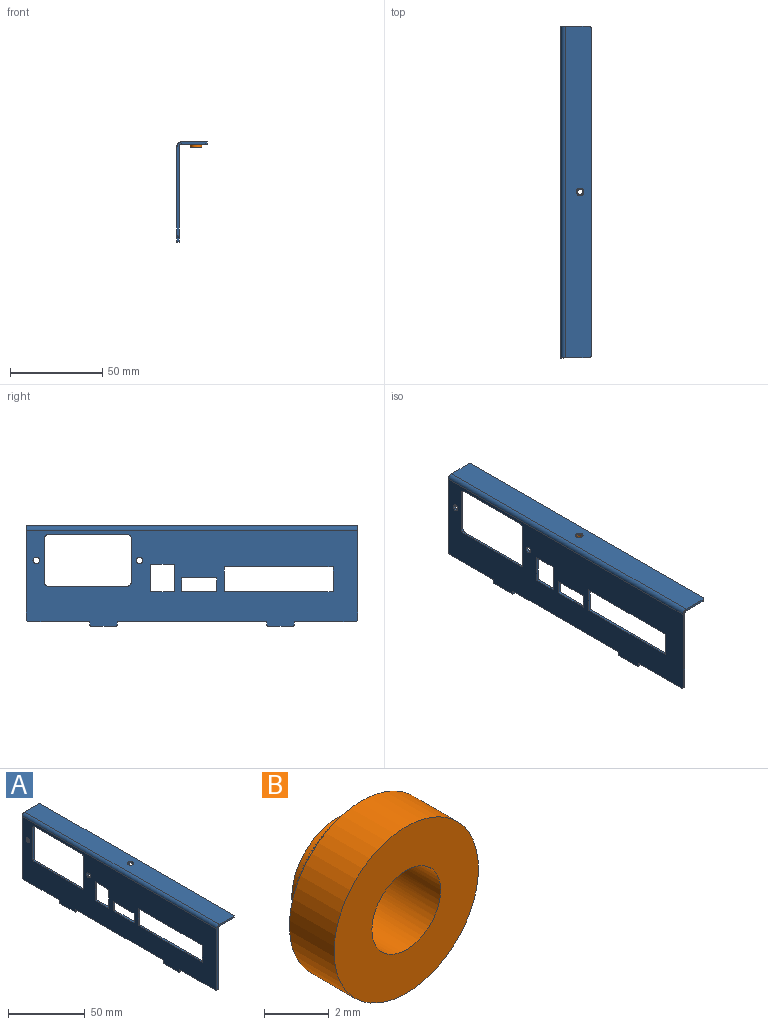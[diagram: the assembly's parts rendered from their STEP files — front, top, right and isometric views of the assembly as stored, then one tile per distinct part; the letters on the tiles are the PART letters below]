
ASSEMBLY  parts=2 mates=1
PART A: 53 faces, bbox 16.4x180x54.3 mm
  f0: plane 15x1.2mm, normal (0,1,0), area 18mm2, adj f1,f32,f33,f34
  f1: plane 12.7x1.2mm, normal (0,0,1), area 15.2mm2, adj f0,f2,f33,f34
  f2: plane 15x1.2mm, normal (0,-1,0), area 18mm2, adj f1,f32,f33,f34
  f3: plane 59x1.2mm, normal (0,0,1), area 70.8mm2, adj f4,f31,f33,f34
  f4: plane 13.5x1.2mm, normal (0,-1,0), area 16.2mm2, adj f3,f5,f33,f34
  f5: plane 59x1.2mm, normal (0,0,-1), area 70.8mm2, adj f4,f31,f33,f34
  f6: cylinder r=2mm len=2mm, axis (1,0,0), area 3.8mm2, adj f7,f28,f33,f34
  f7: plane 43x1.2mm, normal (0,0,1), area 51.6mm2, adj f6,f8,f33,f34
  f8: cylinder r=2mm len=2mm, axis (1,0,0), area 3.8mm2, adj f7,f9,f33,f34
  f9: plane 24x1.2mm, normal (0,-1,0), area 28.8mm2, adj f8,f10,f33,f34
  f10: cylinder r=2mm len=2mm, axis (1,0,0), area 3.8mm2, adj f9,f11,f33,f34
  f11: plane 43x1.2mm, normal (0,0,-1), area 51.6mm2, adj f10,f12,f33,f34
  f12: cylinder r=2mm len=2mm, axis (1,0,0), area 3.8mm2, adj f11,f28,f33,f34
  f13: plane 33x1.2mm, normal (0,0,-1), area 39.6mm2, adj f14,f33,f34,f38
  f14: plane 1.8x1.2mm, normal (0,1,0), area 2.2mm2, adj f13,f33,f34,f36
  f15: plane 14x1.2mm, normal (0,0,-1), area 16.8mm2, adj f33,f34,f35,f36
  f16: plane 1.8x1.2mm, normal (0,-1,0), area 2.2mm2, adj f17,f33,f34,f35
  f17: plane 81x1.2mm, normal (0,0,-1), area 97.2mm2, adj f16,f18,f33,f34
  f18: plane 1.8x1.2mm, normal (0,1,0), area 2.2mm2, adj f17,f33,f34,f39
  f19: plane 14x1.2mm, normal (0,0,-1), area 16.8mm2, adj f33,f34,f39,f40
  f20: plane 1.8x1.2mm, normal (0,-1,0), area 2.2mm2, adj f21,f33,f34,f40
  f21: plane 33x1.2mm, normal (0,0,-1), area 39.6mm2, adj f20,f33,f34,f37
  f22: plane 48.1x1.2mm, normal (0,-1,0), area 57.7mm2, adj f33,f34,f37,f49
  f23: plane 7.5x1.2mm, normal (0,1,0), area 9mm2, adj f24,f26,f33,f34
  f24: plane 19x1.2mm, normal (0,0,1), area 22.8mm2, adj f23,f25,f33,f34
  f25: plane 7.5x1.2mm, normal (0,-1,0), area 9mm2, adj f24,f26,f33,f34
  f26: plane 19x1.2mm, normal (0,0,-1), area 22.8mm2, adj f23,f25,f33,f34
  f27: plane 48.1x1.2mm, normal (0,1,0), area 57.7mm2, adj f33,f34,f38,f50
  f28: plane 24x1.2mm, normal (0,1,0), area 28.8mm2, adj f6,f12,f33,f34
  f29: cylinder r=1.75mm len=3.5mm, axis (1,0,0), area 13.2mm2, adj f33,f34
  f30: cylinder r=1.75mm len=3.5mm, axis (1,0,0), area 13.2mm2, adj f33,f34
  f31: plane 13.5x1.2mm, normal (0,1,0), area 16.2mm2, adj f3,f5,f33,f34
  f32: plane 12.7x1.2mm, normal (0,0,-1), area 15.2mm2, adj f0,f2,f33,f34
  f33: plane 180x51.9mm, normal (-1,0,0), area 6534.5mm2, adj f0,f1,f2,f3,f4,f5,f6,f7
  f34: plane 180x51.9mm, normal (1,0,0), area 6534.5mm2, adj f0,f1,f2,f3,f4,f5,f6,f7
  f35: cylinder r=0.5mm len=1.2mm, axis (1,0,0), area 0.9mm2, adj f15,f16,f33,f34
  f36: cylinder r=0.5mm len=1.2mm, axis (-1,0,0), area 0.9mm2, adj f14,f15,f33,f34
  f37: cylinder r=1.5mm len=1.5mm, axis (1,0,0), area 2.8mm2, adj f21,f22,f33,f34
  f38: cylinder r=1.5mm len=1.5mm, axis (1,0,0), area 2.8mm2, adj f13,f27,f33,f34
  f39: cylinder r=0.5mm len=1.2mm, axis (-1,0,0), area 0.9mm2, adj f18,f19,f33,f34
  f40: cylinder r=0.5mm len=1.2mm, axis (1,0,0), area 0.9mm2, adj f19,f20,f33,f34
  f41: plane 178x1.2mm, normal (1,0,0), area 213.6mm2, adj f45,f46,f47,f48
  f42: plane 13x1.2mm, normal (0,1,0), area 15.6mm2, adj f45,f46,f48,f50
  f43: cylinder r=2.11mm len=4.22mm, axis (0,0,1), area 15.9mm2, adj f45,f46
  f44: plane 13x1.2mm, normal (0,-1,0), area 15.6mm2, adj f45,f46,f47,f49
  f45: plane 180x14mm, normal (0,0,1), area 2505.6mm2, adj f41,f42,f43,f44,f47,f48,f51
  f46: plane 180x14mm, normal (0,0,-1), area 2505.6mm2, adj f41,f42,f43,f44,f47,f48,f52
  f47: cylinder r=1mm len=1.2mm, axis (0,0,-1), area 1.9mm2, adj f41,f44,f45,f46
  f48: cylinder r=1mm len=1.2mm, axis (0,0,-1), area 1.9mm2, adj f41,f42,f45,f46
  f49: plane 2.4x2.4mm, normal (0,-1,0), area 3.4mm2, adj f22,f44,f51,f52
  f50: plane 2.4x2.4mm, normal (0,1,0), area 3.4mm2, adj f27,f42,f51,f52
  f51: cylinder r=2.4mm len=180mm, axis (0,-1,0), area 678.6mm2, adj f33,f45,f49,f50
  f52: cylinder r=1.2mm len=180mm, axis (0,-1,0), area 339.3mm2, adj f34,f46,f49,f50
PART B: 307 faces, bbox 6.3x3x6.3 mm
  f0: plane 5.01x5.01mm, normal (0,1,0), area 6.3mm2, adj f5,f6,f7,f8,f9,f10,f11,f12
  f1: plane 6.3x6.3mm, normal (0,1,0), area 12.3mm2, adj f3,f5,f6,f7,f8,f9,f10,f11
  f2: plane 6.3x6.3mm, normal (0,-1,0), area 24.1mm2, adj f3,f4
  f3: cylinder r=3.15mm len=6.3mm, axis (0,1,0), area 38.6mm2, adj f1,f2
  f4: cylinder r=1.5mm len=3mm, axis (0,1,0), area 28.2mm2, adj f2,f305
  f5: plane 0.5x0.1mm, normal (-0.89,0,0.45), area 0.1mm2, adj f0,f1,f6,f7
  f6: plane 0.5x0.1mm, normal (0.89,0,0.45), area 0.1mm2, adj f0,f1,f5,f8
  f7: plane 0.5x0.11mm, normal (0.91,0,0.41), area 0.1mm2, adj f0,f1,f5,f9
  f8: plane 0.5x0.11mm, normal (-0.91,0,0.41), area 0.1mm2, adj f0,f1,f6,f304
  f9: plane 0.5x0.1mm, normal (-0.87,0,0.49), area 0.1mm2, adj f0,f1,f7,f11
  f10: plane 0.5x0.1mm, normal (-0.85,0,0.52), area 0.1mm2, adj f0,f1,f11,f13
  f11: plane 0.5x0.11mm, normal (0.93,0,0.37), area 0.1mm2, adj f0,f1,f9,f10
  f12: plane 0.5x0.1mm, normal (-0.83,0,0.56), area 0.1mm2, adj f0,f1,f13,f15
  f13: plane 0.5x0.11mm, normal (0.94,0,0.34), area 0.1mm2, adj f0,f1,f10,f12
  f14: plane 0.5x0.09mm, normal (-0.81,0,0.59), area 0.1mm2, adj f0,f1,f15,f17
  f15: plane 0.5x0.11mm, normal (0.96,0,0.3), area 0.1mm2, adj f0,f1,f12,f14
  f16: plane 0.5x0.09mm, normal (-0.78,0,0.63), area 0.1mm2, adj f0,f1,f17,f19
  f17: plane 0.5x0.11mm, normal (0.97,0,0.26), area 0.1mm2, adj f0,f1,f14,f16
  f18: plane 0.5x0.09mm, normal (-0.75,0,0.66), area 0.1mm2, adj f0,f1,f19,f21
  f19: plane 0.5x0.11mm, normal (0.98,0,0.21), area 0.1mm2, adj f0,f1,f16,f18
  f20: plane 0.5x0.08mm, normal (-0.72,0,0.69), area 0.1mm2, adj f0,f1,f21,f23
  f21: plane 0.5x0.11mm, normal (0.98,0,0.17), area 0.1mm2, adj f0,f1,f18,f20
  f22: plane 0.5x0.08mm, normal (-0.69,0,0.72), area 0.1mm2, adj f0,f1,f23,f25
  f23: plane 0.5x0.12mm, normal (0.99,0,0.13), area 0.1mm2, adj f0,f1,f20,f22
  f24: plane 0.5x0.09mm, normal (-0.66,0,0.75), area 0.1mm2, adj f0,f1,f25,f27
  f25: plane 0.5x0.12mm, normal (1,0,0.09), area 0.1mm2, adj f0,f1,f22,f24
  f26: plane 0.5x0.09mm, normal (-0.63,0,0.77), area 0.1mm2, adj f0,f1,f27,f29
  f27: plane 0.5x0.12mm, normal (1,0,0.05), area 0.1mm2, adj f0,f1,f24,f26
  f28: plane 0.5x0.09mm, normal (-0.6,0,0.8), area 0.1mm2, adj f0,f1,f29,f31
  f29: plane 0.5x0.12mm, normal (1,0,0.01), area 0.1mm2, adj f0,f1,f26,f28
  f30: plane 0.5x0.1mm, normal (-0.57,0,0.82), area 0.1mm2, adj f0,f1,f31,f33
  f31: plane 0.5x0.12mm, normal (1,0,-0.04), area 0.1mm2, adj f0,f1,f28,f30
  f32: plane 0.5x0.1mm, normal (-0.53,0,0.85), area 0.1mm2, adj f0,f1,f33,f35
  f33: plane 0.5x0.12mm, normal (1,0,-0.08), area 0.1mm2, adj f0,f1,f30,f32
  f34: plane 0.5x0.1mm, normal (-0.49,0,0.87), area 0.1mm2, adj f0,f1,f35,f37
  f35: plane 0.5x0.12mm, normal (0.99,0,-0.12), area 0.1mm2, adj f0,f1,f32,f34
  f36: plane 0.5x0.1mm, normal (-0.46,0,0.89), area 0.1mm2, adj f0,f1,f37,f39
  f37: plane 0.5x0.12mm, normal (0.99,0,-0.16), area 0.1mm2, adj f0,f1,f34,f36
  f38: plane 0.5x0.11mm, normal (-0.42,0,0.91), area 0.1mm2, adj f0,f1,f39,f41
  f39: plane 0.5x0.11mm, normal (0.98,0,-0.2), area 0.1mm2, adj f0,f1,f36,f38
  f40: plane 0.5x0.11mm, normal (-0.38,0,0.92), area 0.1mm2, adj f0,f1,f41,f43
  f41: plane 0.5x0.11mm, normal (0.97,0,-0.24), area 0.1mm2, adj f0,f1,f38,f40
  f42: plane 0.5x0.11mm, normal (-0.34,0,0.94), area 0.1mm2, adj f0,f1,f43,f45
  f43: plane 0.5x0.11mm, normal (0.96,0,-0.28), area 0.1mm2, adj f0,f1,f40,f42
  f44: plane 0.5x0.11mm, normal (-0.3,0,0.95), area 0.1mm2, adj f0,f1,f45,f47
  f45: plane 0.5x0.11mm, normal (0.95,0,-0.32), area 0.1mm2, adj f0,f1,f42,f44
  f46: plane 0.5x0.11mm, normal (-0.26,0,0.96), area 0.1mm2, adj f0,f1,f47,f49
  f47: plane 0.5x0.11mm, normal (0.93,0,-0.36), area 0.1mm2, adj f0,f1,f44,f46
  f48: plane 0.5x0.11mm, normal (-0.22,0,0.98), area 0.1mm2, adj f0,f1,f49,f51
  f49: plane 0.5x0.11mm, normal (0.92,0,-0.4), area 0.1mm2, adj f0,f1,f46,f48
  f50: plane 0.5x0.11mm, normal (-0.18,0,0.98), area 0.1mm2, adj f0,f1,f51,f53
  f51: plane 0.5x0.1mm, normal (0.9,0,-0.44), area 0.1mm2, adj f0,f1,f48,f50
  f52: plane 0.5x0.12mm, normal (-0.14,0,0.99), area 0.1mm2, adj f0,f1,f53,f55
  f53: plane 0.5x0.1mm, normal (0.88,0,-0.48), area 0.1mm2, adj f0,f1,f50,f52
  f54: plane 0.5x0.12mm, normal (-0.1,0,1), area 0.1mm2, adj f0,f1,f55,f57
  f55: plane 0.5x0.1mm, normal (0.86,0,-0.51), area 0.1mm2, adj f0,f1,f52,f54
  f56: plane 0.5x0.12mm, normal (-0.06,0,1), area 0.1mm2, adj f0,f1,f57,f59
  f57: plane 0.5x0.1mm, normal (0.84,0,-0.55), area 0.1mm2, adj f0,f1,f54,f56
  f58: plane 0.5x0.12mm, normal (-0.01,0,1), area 0.1mm2, adj f0,f1,f59,f61
  f59: plane 0.5x0.09mm, normal (0.81,0,-0.58), area 0.1mm2, adj f0,f1,f56,f58
  f60: plane 0.5x0.12mm, normal (0.03,0,1), area 0.1mm2, adj f0,f1,f61,f63
  f61: plane 0.5x0.09mm, normal (0.79,0,-0.62), area 0.1mm2, adj f0,f1,f58,f60
  f62: plane 0.5x0.12mm, normal (0.07,0,1), area 0.1mm2, adj f0,f1,f63,f65
  f63: plane 0.5x0.09mm, normal (0.76,0,-0.65), area 0.1mm2, adj f0,f1,f60,f62
  f64: plane 0.5x0.12mm, normal (0.11,0,0.99), area 0.1mm2, adj f0,f1,f65,f67
  f65: plane 0.5x0.09mm, normal (0.73,0,-0.68), area 0.1mm2, adj f0,f1,f62,f64
  f66: plane 0.5x0.12mm, normal (0.15,0,0.99), area 0.1mm2, adj f0,f1,f67,f69
  f67: plane 0.5x0.08mm, normal (0.7,0,-0.71), area 0.1mm2, adj f0,f1,f64,f66
  f68: plane 0.5x0.11mm, normal (0.19,0,0.98), area 0.1mm2, adj f0,f1,f69,f71
  f69: plane 0.5x0.09mm, normal (0.67,0,-0.74), area 0.1mm2, adj f0,f1,f66,f68
  f70: plane 0.5x0.11mm, normal (0.23,0,0.97), area 0.1mm2, adj f0,f1,f71,f73
  f71: plane 0.5x0.09mm, normal (0.64,0,-0.77), area 0.1mm2, adj f0,f1,f68,f70
  f72: plane 0.5x0.11mm, normal (0.28,0,0.96), area 0.1mm2, adj f0,f1,f73,f75
  f73: plane 0.5x0.09mm, normal (0.61,0,-0.79), area 0.1mm2, adj f0,f1,f70,f72
  f74: plane 0.5x0.11mm, normal (0.32,0,0.95), area 0.1mm2, adj f0,f1,f75,f77
  f75: plane 0.5x0.1mm, normal (0.58,0,-0.82), area 0.1mm2, adj f0,f1,f72,f74
  f76: plane 0.5x0.11mm, normal (0.35,0,0.93), area 0.1mm2, adj f0,f1,f77,f79
  f77: plane 0.5x0.1mm, normal (0.54,0,-0.84), area 0.1mm2, adj f0,f1,f74,f76
  f78: plane 0.5x0.11mm, normal (0.39,0,0.92), area 0.1mm2, adj f0,f1,f79,f81
  f79: plane 0.5x0.1mm, normal (0.51,0,-0.86), area 0.1mm2, adj f0,f1,f76,f78
  f80: plane 0.5x0.11mm, normal (0.43,0,0.9), area 0.1mm2, adj f0,f1,f81,f83
  f81: plane 0.5x0.1mm, normal (0.47,0,-0.88), area 0.1mm2, adj f0,f1,f78,f80
  f82: plane 0.5x0.1mm, normal (0.47,0,0.88), area 0.1mm2, adj f0,f1,f83,f85
  f83: plane 0.5x0.11mm, normal (0.43,0,-0.9), area 0.1mm2, adj f0,f1,f80,f82
  f84: plane 0.5x0.1mm, normal (0.51,0,0.86), area 0.1mm2, adj f0,f1,f85,f87
  f85: plane 0.5x0.11mm, normal (0.39,0,-0.92), area 0.1mm2, adj f0,f1,f82,f84
  f86: plane 0.5x0.1mm, normal (0.54,0,0.84), area 0.1mm2, adj f0,f1,f87,f89
  f87: plane 0.5x0.11mm, normal (0.35,0,-0.93), area 0.1mm2, adj f0,f1,f84,f86
  f88: plane 0.5x0.1mm, normal (0.58,0,0.82), area 0.1mm2, adj f0,f1,f89,f91
  f89: plane 0.5x0.11mm, normal (0.32,0,-0.95), area 0.1mm2, adj f0,f1,f86,f88
  f90: plane 0.5x0.09mm, normal (0.61,0,0.79), area 0.1mm2, adj f0,f1,f91,f93
  f91: plane 0.5x0.11mm, normal (0.28,0,-0.96), area 0.1mm2, adj f0,f1,f88,f90
  f92: plane 0.5x0.09mm, normal (0.64,0,0.77), area 0.1mm2, adj f0,f1,f93,f95
  f93: plane 0.5x0.11mm, normal (0.23,0,-0.97), area 0.1mm2, adj f0,f1,f90,f92
  f94: plane 0.5x0.09mm, normal (0.67,0,0.74), area 0.1mm2, adj f0,f1,f95,f97
  f95: plane 0.5x0.11mm, normal (0.19,0,-0.98), area 0.1mm2, adj f0,f1,f92,f94
  f96: plane 0.5x0.08mm, normal (0.7,0,0.71), area 0.1mm2, adj f0,f1,f97,f99
  f97: plane 0.5x0.12mm, normal (0.15,0,-0.99), area 0.1mm2, adj f0,f1,f94,f96
  f98: plane 0.5x0.09mm, normal (0.73,0,0.68), area 0.1mm2, adj f0,f1,f99,f101
  f99: plane 0.5x0.12mm, normal (0.11,0,-0.99), area 0.1mm2, adj f0,f1,f96,f98
  f100: plane 0.5x0.09mm, normal (0.76,0,0.65), area 0.1mm2, adj f0,f1,f101,f103
  f101: plane 0.5x0.12mm, normal (0.07,0,-1), area 0.1mm2, adj f0,f1,f98,f100
  f102: plane 0.5x0.09mm, normal (0.79,0,0.62), area 0.1mm2, adj f0,f1,f103,f105
  f103: plane 0.5x0.12mm, normal (0.03,0,-1), area 0.1mm2, adj f0,f1,f100,f102
  f104: plane 0.5x0.09mm, normal (0.81,0,0.58), area 0.1mm2, adj f0,f1,f105,f107
  f105: plane 0.5x0.12mm, normal (-0.01,0,-1), area 0.1mm2, adj f0,f1,f102,f104
  f106: plane 0.5x0.1mm, normal (0.84,0,0.55), area 0.1mm2, adj f0,f1,f107,f109
  f107: plane 0.5x0.12mm, normal (-0.06,0,-1), area 0.1mm2, adj f0,f1,f104,f106
  f108: plane 0.5x0.1mm, normal (0.86,0,0.51), area 0.1mm2, adj f0,f1,f109,f111
  f109: plane 0.5x0.12mm, normal (-0.1,0,-1), area 0.1mm2, adj f0,f1,f106,f108
  f110: plane 0.5x0.1mm, normal (0.88,0,0.48), area 0.1mm2, adj f0,f1,f111,f113
  f111: plane 0.5x0.12mm, normal (-0.14,0,-0.99), area 0.1mm2, adj f0,f1,f108,f110
  f112: plane 0.5x0.1mm, normal (0.9,0,0.44), area 0.1mm2, adj f0,f1,f113,f115
  f113: plane 0.5x0.11mm, normal (-0.18,0,-0.98), area 0.1mm2, adj f0,f1,f110,f112
  f114: plane 0.5x0.11mm, normal (0.92,0,0.4), area 0.1mm2, adj f0,f1,f115,f117
  f115: plane 0.5x0.11mm, normal (-0.22,0,-0.98), area 0.1mm2, adj f0,f1,f112,f114
  f116: plane 0.5x0.11mm, normal (0.93,0,0.36), area 0.1mm2, adj f0,f1,f117,f119
  f117: plane 0.5x0.11mm, normal (-0.26,0,-0.96), area 0.1mm2, adj f0,f1,f114,f116
  f118: plane 0.5x0.11mm, normal (0.95,0,0.32), area 0.1mm2, adj f0,f1,f119,f121
  f119: plane 0.5x0.11mm, normal (-0.3,0,-0.95), area 0.1mm2, adj f0,f1,f116,f118
  f120: plane 0.5x0.11mm, normal (0.96,0,0.28), area 0.1mm2, adj f0,f1,f121,f123
  f121: plane 0.5x0.11mm, normal (-0.34,0,-0.94), area 0.1mm2, adj f0,f1,f118,f120
  f122: plane 0.5x0.11mm, normal (0.97,0,0.24), area 0.1mm2, adj f0,f1,f123,f125
  f123: plane 0.5x0.11mm, normal (-0.38,0,-0.92), area 0.1mm2, adj f0,f1,f120,f122
  f124: plane 0.5x0.11mm, normal (0.98,0,0.2), area 0.1mm2, adj f0,f1,f125,f127
  f125: plane 0.5x0.11mm, normal (-0.42,0,-0.91), area 0.1mm2, adj f0,f1,f122,f124
  f126: plane 0.5x0.12mm, normal (0.99,0,0.16), area 0.1mm2, adj f0,f1,f127,f129
  f127: plane 0.5x0.1mm, normal (-0.46,0,-0.89), area 0.1mm2, adj f0,f1,f124,f126
  f128: plane 0.5x0.12mm, normal (0.99,0,0.12), area 0.1mm2, adj f0,f1,f129,f131
  f129: plane 0.5x0.1mm, normal (-0.49,0,-0.87), area 0.1mm2, adj f0,f1,f126,f128
  f130: plane 0.5x0.12mm, normal (1,0,0.08), area 0.1mm2, adj f0,f1,f131,f133
  f131: plane 0.5x0.1mm, normal (-0.53,0,-0.85), area 0.1mm2, adj f0,f1,f128,f130
  f132: plane 0.5x0.12mm, normal (1,0,0.04), area 0.1mm2, adj f0,f1,f133,f135
  f133: plane 0.5x0.1mm, normal (-0.57,0,-0.82), area 0.1mm2, adj f0,f1,f130,f132
  f134: plane 0.5x0.12mm, normal (1,0,-0.01), area 0.1mm2, adj f0,f1,f135,f137
  f135: plane 0.5x0.09mm, normal (-0.6,0,-0.8), area 0.1mm2, adj f0,f1,f132,f134
  f136: plane 0.5x0.12mm, normal (1,0,-0.05), area 0.1mm2, adj f0,f1,f137,f139
  f137: plane 0.5x0.09mm, normal (-0.63,0,-0.77), area 0.1mm2, adj f0,f1,f134,f136
  f138: plane 0.5x0.12mm, normal (1,0,-0.09), area 0.1mm2, adj f0,f1,f139,f141
  f139: plane 0.5x0.09mm, normal (-0.66,0,-0.75), area 0.1mm2, adj f0,f1,f136,f138
  f140: plane 0.5x0.12mm, normal (0.99,0,-0.13), area 0.1mm2, adj f0,f1,f141,f143
  f141: plane 0.5x0.08mm, normal (-0.69,0,-0.72), area 0.1mm2, adj f0,f1,f138,f140
  f142: plane 0.5x0.11mm, normal (0.98,0,-0.17), area 0.1mm2, adj f0,f1,f143,f145
  f143: plane 0.5x0.08mm, normal (-0.72,0,-0.69), area 0.1mm2, adj f0,f1,f140,f142
  f144: plane 0.5x0.11mm, normal (0.98,0,-0.21), area 0.1mm2, adj f0,f1,f145,f147
  f145: plane 0.5x0.09mm, normal (-0.75,0,-0.66), area 0.1mm2, adj f0,f1,f142,f144
  f146: plane 0.5x0.11mm, normal (0.97,0,-0.26), area 0.1mm2, adj f0,f1,f147,f149
  f147: plane 0.5x0.09mm, normal (-0.78,0,-0.63), area 0.1mm2, adj f0,f1,f144,f146
  f148: plane 0.5x0.11mm, normal (0.96,0,-0.3), area 0.1mm2, adj f0,f1,f149,f151
  f149: plane 0.5x0.09mm, normal (-0.81,0,-0.59), area 0.1mm2, adj f0,f1,f146,f148
  f150: plane 0.5x0.11mm, normal (0.94,0,-0.34), area 0.1mm2, adj f0,f1,f151,f153
  f151: plane 0.5x0.1mm, normal (-0.83,0,-0.56), area 0.1mm2, adj f0,f1,f148,f150
  f152: plane 0.5x0.11mm, normal (0.93,0,-0.37), area 0.1mm2, adj f0,f1,f153,f155
  f153: plane 0.5x0.1mm, normal (-0.85,0,-0.52), area 0.1mm2, adj f0,f1,f150,f152
  f154: plane 0.5x0.11mm, normal (0.91,0,-0.41), area 0.1mm2, adj f0,f1,f155,f157
  f155: plane 0.5x0.1mm, normal (-0.87,0,-0.49), area 0.1mm2, adj f0,f1,f152,f154
  f156: plane 0.5x0.1mm, normal (0.89,0,-0.45), area 0.1mm2, adj f0,f1,f157,f159
  f157: plane 0.5x0.1mm, normal (-0.89,0,-0.45), area 0.1mm2, adj f0,f1,f154,f156
  f158: plane 0.5x0.1mm, normal (0.87,0,-0.49), area 0.1mm2, adj f0,f1,f159,f161
  f159: plane 0.5x0.11mm, normal (-0.91,0,-0.41), area 0.1mm2, adj f0,f1,f156,f158
  f160: plane 0.5x0.1mm, normal (0.85,0,-0.52), area 0.1mm2, adj f0,f1,f161,f163
  f161: plane 0.5x0.11mm, normal (-0.93,0,-0.37), area 0.1mm2, adj f0,f1,f158,f160
  f162: plane 0.5x0.1mm, normal (0.83,0,-0.56), area 0.1mm2, adj f0,f1,f163,f165
  f163: plane 0.5x0.11mm, normal (-0.94,0,-0.34), area 0.1mm2, adj f0,f1,f160,f162
  f164: plane 0.5x0.09mm, normal (0.81,0,-0.59), area 0.1mm2, adj f0,f1,f165,f167
  f165: plane 0.5x0.11mm, normal (-0.96,0,-0.3), area 0.1mm2, adj f0,f1,f162,f164
  f166: plane 0.5x0.09mm, normal (0.78,0,-0.63), area 0.1mm2, adj f0,f1,f167,f169
  f167: plane 0.5x0.11mm, normal (-0.97,0,-0.26), area 0.1mm2, adj f0,f1,f164,f166
  f168: plane 0.5x0.09mm, normal (0.75,0,-0.66), area 0.1mm2, adj f0,f1,f169,f171
  f169: plane 0.5x0.11mm, normal (-0.98,0,-0.21), area 0.1mm2, adj f0,f1,f166,f168
  f170: plane 0.5x0.08mm, normal (0.72,0,-0.69), area 0.1mm2, adj f0,f1,f171,f173
  f171: plane 0.5x0.11mm, normal (-0.98,0,-0.17), area 0.1mm2, adj f0,f1,f168,f170
  f172: plane 0.5x0.08mm, normal (0.69,0,-0.72), area 0.1mm2, adj f0,f1,f173,f175
  f173: plane 0.5x0.12mm, normal (-0.99,0,-0.13), area 0.1mm2, adj f0,f1,f170,f172
  f174: plane 0.5x0.09mm, normal (0.66,0,-0.75), area 0.1mm2, adj f0,f1,f175,f177
  f175: plane 0.5x0.12mm, normal (-1,0,-0.09), area 0.1mm2, adj f0,f1,f172,f174
  f176: plane 0.5x0.09mm, normal (0.63,0,-0.77), area 0.1mm2, adj f0,f1,f177,f179
  f177: plane 0.5x0.12mm, normal (-1,0,-0.05), area 0.1mm2, adj f0,f1,f174,f176
  f178: plane 0.5x0.09mm, normal (0.6,0,-0.8), area 0.1mm2, adj f0,f1,f179,f181
  f179: plane 0.5x0.12mm, normal (-1,0,-0.01), area 0.1mm2, adj f0,f1,f176,f178
  f180: plane 0.5x0.1mm, normal (0.57,0,-0.82), area 0.1mm2, adj f0,f1,f181,f183
  f181: plane 0.5x0.12mm, normal (-1,0,0.04), area 0.1mm2, adj f0,f1,f178,f180
  f182: plane 0.5x0.1mm, normal (0.53,0,-0.85), area 0.1mm2, adj f0,f1,f183,f185
  f183: plane 0.5x0.12mm, normal (-1,0,0.08), area 0.1mm2, adj f0,f1,f180,f182
  f184: plane 0.5x0.1mm, normal (0.49,0,-0.87), area 0.1mm2, adj f0,f1,f185,f187
  f185: plane 0.5x0.12mm, normal (-0.99,0,0.12), area 0.1mm2, adj f0,f1,f182,f184
  f186: plane 0.5x0.1mm, normal (0.46,0,-0.89), area 0.1mm2, adj f0,f1,f187,f189
  f187: plane 0.5x0.12mm, normal (-0.99,0,0.16), area 0.1mm2, adj f0,f1,f184,f186
  f188: plane 0.5x0.11mm, normal (0.42,0,-0.91), area 0.1mm2, adj f0,f1,f189,f191
  f189: plane 0.5x0.11mm, normal (-0.98,0,0.2), area 0.1mm2, adj f0,f1,f186,f188
  f190: plane 0.5x0.11mm, normal (0.38,0,-0.92), area 0.1mm2, adj f0,f1,f191,f193
  f191: plane 0.5x0.11mm, normal (-0.97,0,0.24), area 0.1mm2, adj f0,f1,f188,f190
  f192: plane 0.5x0.11mm, normal (0.34,0,-0.94), area 0.1mm2, adj f0,f1,f193,f195
  f193: plane 0.5x0.11mm, normal (-0.96,0,0.28), area 0.1mm2, adj f0,f1,f190,f192
  f194: plane 0.5x0.11mm, normal (0.3,0,-0.95), area 0.1mm2, adj f0,f1,f195,f197
  f195: plane 0.5x0.11mm, normal (-0.95,0,0.32), area 0.1mm2, adj f0,f1,f192,f194
  f196: plane 0.5x0.11mm, normal (0.26,0,-0.96), area 0.1mm2, adj f0,f1,f197,f199
  f197: plane 0.5x0.11mm, normal (-0.93,0,0.36), area 0.1mm2, adj f0,f1,f194,f196
  f198: plane 0.5x0.11mm, normal (0.22,0,-0.98), area 0.1mm2, adj f0,f1,f199,f201
  f199: plane 0.5x0.11mm, normal (-0.92,0,0.4), area 0.1mm2, adj f0,f1,f196,f198
  f200: plane 0.5x0.11mm, normal (0.18,0,-0.98), area 0.1mm2, adj f0,f1,f201,f203
  f201: plane 0.5x0.1mm, normal (-0.9,0,0.44), area 0.1mm2, adj f0,f1,f198,f200
  f202: plane 0.5x0.12mm, normal (0.14,0,-0.99), area 0.1mm2, adj f0,f1,f203,f205
  f203: plane 0.5x0.1mm, normal (-0.88,0,0.48), area 0.1mm2, adj f0,f1,f200,f202
  f204: plane 0.5x0.12mm, normal (0.1,0,-1), area 0.1mm2, adj f0,f1,f205,f207
  f205: plane 0.5x0.1mm, normal (-0.86,0,0.51), area 0.1mm2, adj f0,f1,f202,f204
  f206: plane 0.5x0.12mm, normal (0.06,0,-1), area 0.1mm2, adj f0,f1,f207,f209
  f207: plane 0.5x0.1mm, normal (-0.84,0,0.55), area 0.1mm2, adj f0,f1,f204,f206
  f208: plane 0.5x0.12mm, normal (0.01,0,-1), area 0.1mm2, adj f0,f1,f209,f211
  f209: plane 0.5x0.09mm, normal (-0.81,0,0.58), area 0.1mm2, adj f0,f1,f206,f208
  f210: plane 0.5x0.12mm, normal (-0.03,0,-1), area 0.1mm2, adj f0,f1,f211,f213
  f211: plane 0.5x0.09mm, normal (-0.79,0,0.62), area 0.1mm2, adj f0,f1,f208,f210
  f212: plane 0.5x0.12mm, normal (-0.07,0,-1), area 0.1mm2, adj f0,f1,f213,f215
  f213: plane 0.5x0.09mm, normal (-0.76,0,0.65), area 0.1mm2, adj f0,f1,f210,f212
  f214: plane 0.5x0.12mm, normal (-0.11,0,-0.99), area 0.1mm2, adj f0,f1,f215,f217
  f215: plane 0.5x0.09mm, normal (-0.73,0,0.68), area 0.1mm2, adj f0,f1,f212,f214
  f216: plane 0.5x0.12mm, normal (-0.15,0,-0.99), area 0.1mm2, adj f0,f1,f217,f219
  f217: plane 0.5x0.08mm, normal (-0.7,0,0.71), area 0.1mm2, adj f0,f1,f214,f216
  f218: plane 0.5x0.11mm, normal (-0.19,0,-0.98), area 0.1mm2, adj f0,f1,f219,f221
  f219: plane 0.5x0.09mm, normal (-0.67,0,0.74), area 0.1mm2, adj f0,f1,f216,f218
  f220: plane 0.5x0.11mm, normal (-0.23,0,-0.97), area 0.1mm2, adj f0,f1,f221,f223
  f221: plane 0.5x0.09mm, normal (-0.64,0,0.77), area 0.1mm2, adj f0,f1,f218,f220
  f222: plane 0.5x0.11mm, normal (-0.28,0,-0.96), area 0.1mm2, adj f0,f1,f223,f225
  f223: plane 0.5x0.09mm, normal (-0.61,0,0.79), area 0.1mm2, adj f0,f1,f220,f222
  f224: plane 0.5x0.11mm, normal (-0.32,0,-0.95), area 0.1mm2, adj f0,f1,f225,f227
  f225: plane 0.5x0.1mm, normal (-0.58,0,0.82), area 0.1mm2, adj f0,f1,f222,f224
  f226: plane 0.5x0.11mm, normal (-0.35,0,-0.93), area 0.1mm2, adj f0,f1,f227,f229
  f227: plane 0.5x0.1mm, normal (-0.54,0,0.84), area 0.1mm2, adj f0,f1,f224,f226
  f228: plane 0.5x0.11mm, normal (-0.39,0,-0.92), area 0.1mm2, adj f0,f1,f229,f231
  f229: plane 0.5x0.1mm, normal (-0.51,0,0.86), area 0.1mm2, adj f0,f1,f226,f228
  f230: plane 0.5x0.11mm, normal (-0.43,0,-0.9), area 0.1mm2, adj f0,f1,f231,f233
  f231: plane 0.5x0.1mm, normal (-0.47,0,0.88), area 0.1mm2, adj f0,f1,f228,f230
  f232: plane 0.5x0.1mm, normal (-0.47,0,-0.88), area 0.1mm2, adj f0,f1,f233,f235
  f233: plane 0.5x0.11mm, normal (-0.43,0,0.9), area 0.1mm2, adj f0,f1,f230,f232
  f234: plane 0.5x0.1mm, normal (-0.51,0,-0.86), area 0.1mm2, adj f0,f1,f235,f237
  f235: plane 0.5x0.11mm, normal (-0.39,0,0.92), area 0.1mm2, adj f0,f1,f232,f234
  f236: plane 0.5x0.1mm, normal (-0.54,0,-0.84), area 0.1mm2, adj f0,f1,f237,f239
  f237: plane 0.5x0.11mm, normal (-0.35,0,0.93), area 0.1mm2, adj f0,f1,f234,f236
  f238: plane 0.5x0.1mm, normal (-0.58,0,-0.82), area 0.1mm2, adj f0,f1,f239,f241
  f239: plane 0.5x0.11mm, normal (-0.32,0,0.95), area 0.1mm2, adj f0,f1,f236,f238
  f240: plane 0.5x0.09mm, normal (-0.61,0,-0.79), area 0.1mm2, adj f0,f1,f241,f243
  f241: plane 0.5x0.11mm, normal (-0.28,0,0.96), area 0.1mm2, adj f0,f1,f238,f240
  f242: plane 0.5x0.09mm, normal (-0.64,0,-0.77), area 0.1mm2, adj f0,f1,f243,f245
  f243: plane 0.5x0.11mm, normal (-0.23,0,0.97), area 0.1mm2, adj f0,f1,f240,f242
  f244: plane 0.5x0.09mm, normal (-0.67,0,-0.74), area 0.1mm2, adj f0,f1,f245,f247
  f245: plane 0.5x0.11mm, normal (-0.19,0,0.98), area 0.1mm2, adj f0,f1,f242,f244
  f246: plane 0.5x0.08mm, normal (-0.7,0,-0.71), area 0.1mm2, adj f0,f1,f247,f249
  f247: plane 0.5x0.12mm, normal (-0.15,0,0.99), area 0.1mm2, adj f0,f1,f244,f246
  f248: plane 0.5x0.09mm, normal (-0.73,0,-0.68), area 0.1mm2, adj f0,f1,f249,f251
  f249: plane 0.5x0.12mm, normal (-0.11,0,0.99), area 0.1mm2, adj f0,f1,f246,f248
  f250: plane 0.5x0.09mm, normal (-0.76,0,-0.65), area 0.1mm2, adj f0,f1,f251,f253
  f251: plane 0.5x0.12mm, normal (-0.07,0,1), area 0.1mm2, adj f0,f1,f248,f250
  f252: plane 0.5x0.09mm, normal (-0.79,0,-0.62), area 0.1mm2, adj f0,f1,f253,f255
  f253: plane 0.5x0.12mm, normal (-0.03,0,1), area 0.1mm2, adj f0,f1,f250,f252
  f254: plane 0.5x0.09mm, normal (-0.81,0,-0.58), area 0.1mm2, adj f0,f1,f255,f257
  f255: plane 0.5x0.12mm, normal (0.01,0,1), area 0.1mm2, adj f0,f1,f252,f254
  f256: plane 0.5x0.1mm, normal (-0.84,0,-0.55), area 0.1mm2, adj f0,f1,f257,f259
  f257: plane 0.5x0.12mm, normal (0.06,0,1), area 0.1mm2, adj f0,f1,f254,f256
  f258: plane 0.5x0.1mm, normal (-0.86,0,-0.51), area 0.1mm2, adj f0,f1,f259,f261
  f259: plane 0.5x0.12mm, normal (0.1,0,1), area 0.1mm2, adj f0,f1,f256,f258
  f260: plane 0.5x0.1mm, normal (-0.88,0,-0.48), area 0.1mm2, adj f0,f1,f261,f263
  f261: plane 0.5x0.12mm, normal (0.14,0,0.99), area 0.1mm2, adj f0,f1,f258,f260
  f262: plane 0.5x0.1mm, normal (-0.9,0,-0.44), area 0.1mm2, adj f0,f1,f263,f265
  f263: plane 0.5x0.11mm, normal (0.18,0,0.98), area 0.1mm2, adj f0,f1,f260,f262
  f264: plane 0.5x0.11mm, normal (-0.92,0,-0.4), area 0.1mm2, adj f0,f1,f265,f267
  f265: plane 0.5x0.11mm, normal (0.22,0,0.98), area 0.1mm2, adj f0,f1,f262,f264
  f266: plane 0.5x0.11mm, normal (-0.93,0,-0.36), area 0.1mm2, adj f0,f1,f267,f269
  f267: plane 0.5x0.11mm, normal (0.26,0,0.96), area 0.1mm2, adj f0,f1,f264,f266
  f268: plane 0.5x0.11mm, normal (-0.95,0,-0.32), area 0.1mm2, adj f0,f1,f269,f271
  f269: plane 0.5x0.11mm, normal (0.3,0,0.95), area 0.1mm2, adj f0,f1,f266,f268
  f270: plane 0.5x0.11mm, normal (-0.96,0,-0.28), area 0.1mm2, adj f0,f1,f271,f273
  f271: plane 0.5x0.11mm, normal (0.34,0,0.94), area 0.1mm2, adj f0,f1,f268,f270
  f272: plane 0.5x0.11mm, normal (-0.97,0,-0.24), area 0.1mm2, adj f0,f1,f273,f275
  f273: plane 0.5x0.11mm, normal (0.38,0,0.92), area 0.1mm2, adj f0,f1,f270,f272
  f274: plane 0.5x0.11mm, normal (-0.98,0,-0.2), area 0.1mm2, adj f0,f1,f275,f277
  f275: plane 0.5x0.11mm, normal (0.42,0,0.91), area 0.1mm2, adj f0,f1,f272,f274
  f276: plane 0.5x0.12mm, normal (-0.99,0,-0.16), area 0.1mm2, adj f0,f1,f277,f279
  f277: plane 0.5x0.1mm, normal (0.46,0,0.89), area 0.1mm2, adj f0,f1,f274,f276
  f278: plane 0.5x0.12mm, normal (-0.99,0,-0.12), area 0.1mm2, adj f0,f1,f279,f281
  f279: plane 0.5x0.1mm, normal (0.49,0,0.87), area 0.1mm2, adj f0,f1,f276,f278
  f280: plane 0.5x0.12mm, normal (-1,0,-0.08), area 0.1mm2, adj f0,f1,f281,f283
  f281: plane 0.5x0.1mm, normal (0.53,0,0.85), area 0.1mm2, adj f0,f1,f278,f280
  f282: plane 0.5x0.12mm, normal (-1,0,-0.04), area 0.1mm2, adj f0,f1,f283,f285
  f283: plane 0.5x0.1mm, normal (0.57,0,0.82), area 0.1mm2, adj f0,f1,f280,f282
  f284: plane 0.5x0.12mm, normal (-1,0,0.01), area 0.1mm2, adj f0,f1,f285,f287
  f285: plane 0.5x0.09mm, normal (0.6,0,0.8), area 0.1mm2, adj f0,f1,f282,f284
  f286: plane 0.5x0.12mm, normal (-1,0,0.05), area 0.1mm2, adj f0,f1,f287,f289
  f287: plane 0.5x0.09mm, normal (0.63,0,0.77), area 0.1mm2, adj f0,f1,f284,f286
  f288: plane 0.5x0.12mm, normal (-1,0,0.09), area 0.1mm2, adj f0,f1,f289,f291
  f289: plane 0.5x0.09mm, normal (0.66,0,0.75), area 0.1mm2, adj f0,f1,f286,f288
  f290: plane 0.5x0.12mm, normal (-0.99,0,0.13), area 0.1mm2, adj f0,f1,f291,f293
  f291: plane 0.5x0.08mm, normal (0.69,0,0.72), area 0.1mm2, adj f0,f1,f288,f290
  f292: plane 0.5x0.11mm, normal (-0.98,0,0.17), area 0.1mm2, adj f0,f1,f293,f295
  f293: plane 0.5x0.08mm, normal (0.72,0,0.69), area 0.1mm2, adj f0,f1,f290,f292
  f294: plane 0.5x0.11mm, normal (-0.98,0,0.21), area 0.1mm2, adj f0,f1,f295,f297
  f295: plane 0.5x0.09mm, normal (0.75,0,0.66), area 0.1mm2, adj f0,f1,f292,f294
  f296: plane 0.5x0.11mm, normal (-0.97,0,0.26), area 0.1mm2, adj f0,f1,f297,f299
  f297: plane 0.5x0.09mm, normal (0.78,0,0.63), area 0.1mm2, adj f0,f1,f294,f296
  f298: plane 0.5x0.11mm, normal (-0.96,0,0.3), area 0.1mm2, adj f0,f1,f299,f301
  f299: plane 0.5x0.09mm, normal (0.81,0,0.59), area 0.1mm2, adj f0,f1,f296,f298
  f300: plane 0.5x0.11mm, normal (-0.94,0,0.34), area 0.1mm2, adj f0,f1,f301,f303
  f301: plane 0.5x0.1mm, normal (0.83,0,0.56), area 0.1mm2, adj f0,f1,f298,f300
  f302: plane 0.5x0.11mm, normal (-0.93,0,0.37), area 0.1mm2, adj f0,f1,f303,f304
  f303: plane 0.5x0.1mm, normal (0.85,0,0.52), area 0.1mm2, adj f0,f1,f300,f302
  f304: plane 0.5x0.1mm, normal (0.87,0,0.49), area 0.1mm2, adj f0,f1,f8,f302
  f305: plane 4x4mm, normal (0,1,0), area 5.5mm2, adj f4,f306
  f306: cylinder r=2mm len=4mm, axis (0,-1,0), area 6.9mm2, adj f0,f305
PLACE A at identity fixed
PLACE B rot(axis=(1,0,0),90deg) t=(-45.8,0,52.3)mm
MATE fastened B.f3 <-> A.f43  axis (0,0,1) through (-45.8,0,52.3)mm
